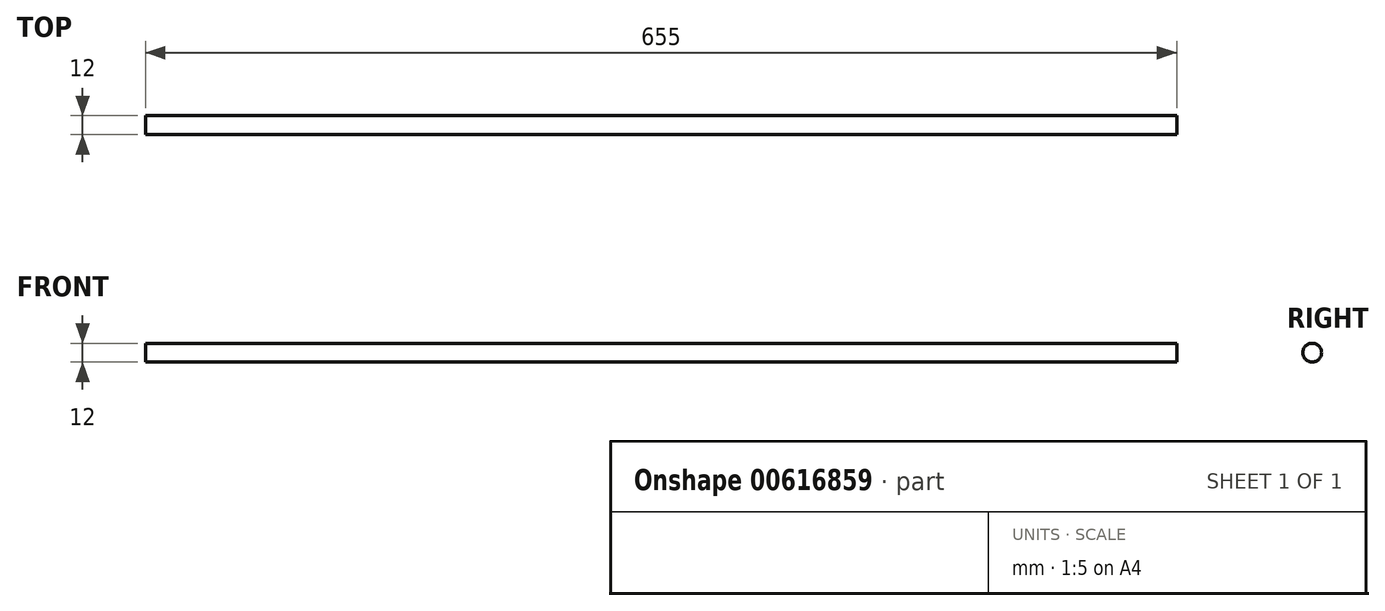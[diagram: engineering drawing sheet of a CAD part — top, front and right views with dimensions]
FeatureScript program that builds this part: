
annotation { "Feature Type Name" : "Feature", "Feature Type Description" : "" }
export const myFeature = defineFeature(function(context is Context, id is Id, definition is map)
    precondition{}
    {
        {
            var Q0;
            Q0=qCreatedBy(makeId("Right.planeOp"),FACE);
            var sketch = newSketch(context, id + "F0", { "sketchPlane" : qUnion([Q0])});
            skCircle(sketch, "E0", {"center": v(0, 0) * mm, "radius": 6 * mm});
            skSolve(sketch);
        }
        {
            var Q0;
            Q0 = qSketchRegion(id + "F0", true);
            extrude(context, id + "F1", {"entities" : qUnion([Q0]), "depth" : 327.5 * mm, "offsetDistance" : 25 * mm, "hasSecondDirection" : true, "secondDirectionOppositeDirection" : true, "secondDirectionDepth" : 327.5 * mm});
        }
    });
